# Revit family: Domotics-DomesticRanges-GEWISS-CHORUS_COMMAND-DIMMER_PUSH_BUTTON
name_source: partatom
category: Apparecchi elettrici
revit_build: Autodesk Revit 2016 (Build: 20161004_0715(x64)
units: mm (PartAtom-declared; Revit-internal decimal feet)

## family parameters
Condiviso = Sì
Host = Superficie
Mantenere orientamento annotazione = Sì
Punto di calcolo locali = Sì
Quota connettore circolare = Usa diametro
Taglio con vuoti quando caricato = Sì
Tipo di parte = Normale

## types (9) — shared parameters
Carico apparente = 0 VA
Catalogue = DOMOTICS
Catalogue Range = CHORUS - DOMESTIC RANGE
IDF = b0176bc3-d912-4049-8e7a-778e5a49908c
IDT = a6fbcf2a-2fdb-4c97-974f-833a3f949291
Immagine tipo = GW14568.jpg
N. poli = 1
Produttore = GEWISS S.p.A.
Prospetto di default = 1219 mm
Technical sheet = https://www.gewiss.com
Tipo simbolo = PULSANTI : DIMMMANOP
Tipo_ = CHORUS DIMMER PULSANTE_GENERICO : GW14574 Regolatore elettronico agitatore aria 230V 55-80VA titanio
URL = https://www.gewiss.com
Version file RFA = 19.0
Volt = 230 V

## per-type parameters (varying)
| type | Colour | Command | Control | Description. | Descrizione | EAN code | Electrocod | Inductive load | Inductive load 230V ac | Load 230V ac | Load type | Modello | No. Chorus modules | No. Chorus modules: | Resistive load | Resistive load 230V ac | SEO | Supply voltage |
| GW14571 - ELEC. PUSHBUTTON REGULATOR 1M TITANIUM |  |  |  |  | ELEC. PUSHBUTTON REGULATOR 1M TITANIUM | 8011564895157 | 0141 |  |  |  |  | GW14571 |  |  |  |  |  |  |
| GW14568 - Electronic regulator with push-button 1M 60-500W Titanium | Titanium | Push-button | Push-button | Push-button dimmer | PUSH-BUTTON ELEC REGULATOR, 1M 60-500W T | 8011564267992 | 0141 | 60 - 500 VA | 60 - 500 VA |  | Resistive/Inductive | GW14568 | 1 | 1 | 60 - 500 W | 60 - 500 W | Dimmer | 230V ac - 50 Hz |
| GW12568 - Electronic regulator with push-button 1M 60-500W Black | Black | Push-button | Push-button | Push-button dimmer | PUSH-BUTTON ELEC REGULATOR 1M 60-500W B | 8011564268302 | 0141 | 60 - 500 VA | 60 - 500 VA |  | Resistive/Inductive | GW12568 | 1 | 1 | 60 - 500 W | 60 - 500 W | Dimmer | 230V ac - 50 Hz |
| GW10571 - ELEC. PUSHBUTTON REGULATOR 1M WHITE |  |  |  |  | ELEC. PUSHBUTTON REGULATOR 1M WHITE | 8011564895126 | 0781 |  |  |  |  | GW10571 |  |  |  |  |  |  |
| GW14574 - Electronic regulator air mover 230V 55-80VA Titanium | Titanium | Push-button | Push-button | Push-button dimmer | ELEC.REGUL.AIR STIRR. 230V 55-80VA CH/TI | 8011564268012 | 0130 |  |  | 55-80 VA | Air agitators | GW14574 | 1 | 1 |  |  | Dimmer | 230V ac - 50 Hz |
| GW12571 - ELEC. PUSHBUTTON REGULATOR 1M BLACK |  |  |  |  | ELEC. PUSHBUTTON REGULATOR 1M BLACK | 8011564895140 | 0141 |  |  |  |  | GW12571 |  |  |  |  |  |  |
| GW10568 - Electronic regulator with push-button 1M 60-500W White | White | Push-button | Push-button | Push-button dimmer | PUSH-BUTTON ELEC REGULATOR 1M 60-500W W | 8011564261105 | 0781 | 60 - 500 VA | 60 - 500 VA |  | Resistive/Inductive | GW10568 | 1 | 1 | 60 - 500 W | 60 - 500 W | Dimmer | 230V ac - 50 Hz |
| GW12574 - Electronic regulator air mover 230V 55-80VA Black | Black | Push-button | Push-button | Push-button dimmer | ELEC.REGUL.AIR STIRR. 230V 55-80VA CH/BK | 8011564268326 | 0130 |  |  | 55-80 VA | Air agitators | GW12574 | 1 | 1 |  |  | Dimmer | 230V ac - 50 Hz |
| GW10574 - Electronic regulator air mover 230V 55-80VA White | White | Push-button | Push-button | Push-button dimmer | ELEC.REGUL. AIR AGIT. 230V 55-80VA CH/WH | 8011564261112 | 0130 |  |  | 55-80 VA | Air agitators | GW10574 | 1 | 1 |  |  | Dimmer | 230V ac - 50 Hz |

## geometry (parser evidence)
native form markers: Sweep x2
no freeform markers — native parametric forms only
